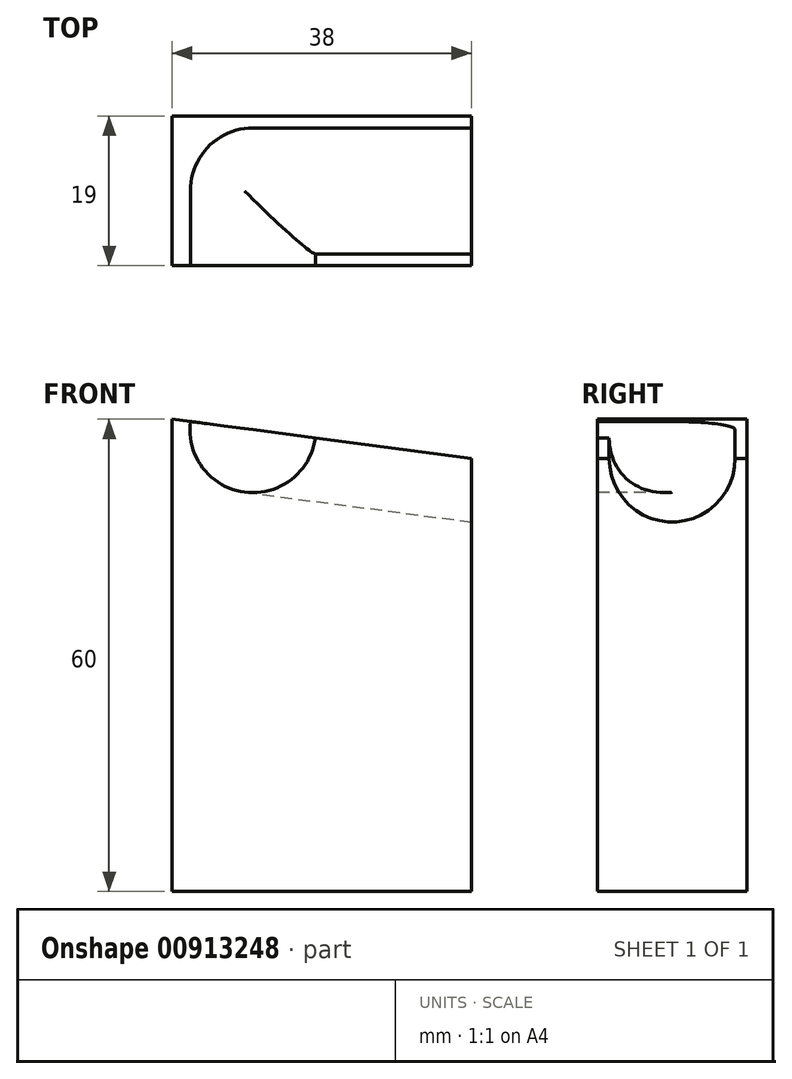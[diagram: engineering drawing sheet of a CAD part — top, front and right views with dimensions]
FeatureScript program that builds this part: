
annotation { "Feature Type Name" : "Feature", "Feature Type Description" : "" }
export const myFeature = defineFeature(function(context is Context, id is Id, definition is map)
    precondition{}
    {
        {
            var Q0;
            Q0=qCreatedBy(makeId("Front.planeOp"),FACE);
            var sketch = newSketch(context, id + "F0", { "sketchPlane" : qUnion([Q0])});
            skLineSegment(sketch, "E0.bottom", {"start": v(0, 0) * mm, "end": v(-38, 0) * mm});
            skLineSegment(sketch, "E0.left", {"start": v(0, 0) * mm, "end": v(0, 55) * mm});
            skLineSegment(sketch, "E0.right", {"start": v(-38, 0) * mm, "end": v(-38, 60) * mm});
            skLineSegment(sketch, "E1", {"start": v(-38, 60) * mm, "end": v(0, 55) * mm});
            skLineSegment(sketch, "E2", {"start": v(0, 55) * mm, "end": v(-4.08, 23.96) * mm, "construction": true});
            skSolve(sketch);
        }
        {
            var Q0;
            Q0 = qSketchRegion(id + "F0", true);
            extrude(context, id + "F1", {"entities" : qUnion([Q0]), "oppositeDirection" : true, "depth" : 19 * mm, "offsetDistance" : 25.4 * mm});
        }
        {
            var Q0;
            Q0=sQuery(id+"F0.wireOp",VERTEX,"E0.left.end");
            var Q1;
            Q1=sQuery(id+"F0.wireOp",VERTEX,"E2.end");
            var Q2;
            Q2=makeQuery(id+"F1.opExtrude","CAP_VERTEX",VERTEX,{"disambiguationData":[OSD([sQuery(id+"F0.wireOp",EDGE,"E0.left"),sQuery(id+"F0.wireOp",EDGE,"E1")])],"isStart":false});
            cPlane(context, id + "F2", {"entities" : qUnion([Q0, Q1, Q2]), "cplaneType" : CPlaneType.THREE_POINT, "offset" : 10 * mm, "width" : 152.4 * mm, "height" : 152.4 * mm});
        }
        {
            var Q0;
            Q0=qCreatedBy(id+"F2.planeOp",FACE);
            var sketch = newSketch(context, id + "F3", { "sketchPlane" : qUnion([Q0])});
            skArc(sketch, "E3", {"start": v(-17.5, 54.53) * mm, "mid": v(-9.5, 46.53) * mm, "end": v(-1.5, 54.53) * mm});
            skLineSegment(sketch, "E4", {"start": v(-1.5, 54.53) * mm, "end": v(-17.5, 54.53) * mm});
            skSolve(sketch);
        }
        {
            var Q0;
            Q0 = qSketchRegion(id + "F3", true);
            extrude(context, id + "F4", {"entities" : qUnion([Q0]), "operationType" : NewBodyOperationType.REMOVE, "endBound" : BoundingType.SYMMETRIC, "depth" : 56 * mm, "offsetDistance" : 25 * mm});
        }
        {
            var Q0;
            Q0=makeQuery(id+"F4.boolean.opBoolean","COPY",FACE,{"derivedFrom":makeQuery(id+"F4.opExtrude","CAP_FACE",FACE,{"disambiguationData":[OSD([sQuery(id+"F3.wireOp",EDGE,"E3"),sQuery(id+"F3.wireOp",EDGE,"E4")])],"isStart":false})});
            cPlane(context, id + "F5", {"entities" : qUnion([Q0]), "cplaneType" : CPlaneType.OFFSET, "offset" : 0 * mm, "width" : 150 * mm, "height" : 150 * mm});
        }
        {
            var Q0;
            Q0=qCreatedBy(id+"F5.planeOp",FACE);
            var sketch = newSketch(context, id + "F6", { "sketchPlane" : qUnion([Q0])});
            skLineSegment(sketch, "E5", {"start": v(1.5, 54.53) * mm, "end": v(0, 54.53) * mm, "construction": true});
            skArc(sketch, "E6", {"start": v(17.5, 54.53) * mm, "mid": v(15.16, 48.87) * mm, "end": v(9.5, 46.53) * mm});
            skLineSegment(sketch, "E7", {"start": v(9.5, 46.53) * mm, "end": v(9.5, 54.53) * mm});
            skLineSegment(sketch, "E8", {"start": v(9.5, 54.53) * mm, "end": v(17.5, 54.53) * mm});
            skSolve(sketch);
        }
        {
            var Q0;
            Q0 = qSketchRegion(id + "F6", true);
            var Q1;
            Q1=sQuery(id+"F6.wireOp",EDGE,"E7");
            revolve(context, id + "F7", {"operationType" : NewBodyOperationType.REMOVE, "surfaceOperationType" : NewSurfaceOperationType.NEW, "entities" : qUnion([Q0]), "axis" : qUnion([Q1]), "revolveType" : RevolveType.FULL, "oppositeDirection" : true});
        }
        {
            var Q0;
            Q0=qCreatedBy(makeId("Front.planeOp"),FACE);
            var sketch = newSketch(context, id + "F8", { "sketchPlane" : qUnion([Q0])});
            skArc(sketch, "E9", {"start": v(-19.83, 57.6) * mm, "mid": v(-28.8, 50.72) * mm, "end": v(-35.7, 59.7) * mm});
            skLineSegment(sketch, "E10", {"start": v(-35.7, 59.7) * mm, "end": v(-19.83, 57.6) * mm});
            skSolve(sketch);
        }
        {
            var Q0;
            Q0 = qSketchRegion(id + "F8", true);
            extrude(context, id + "F9", {"entities" : qUnion([Q0]), "operationType" : NewBodyOperationType.REMOVE, "oppositeDirection" : true, "depth" : 9.5 * mm, "offsetDistance" : 25 * mm});
        }
    });
